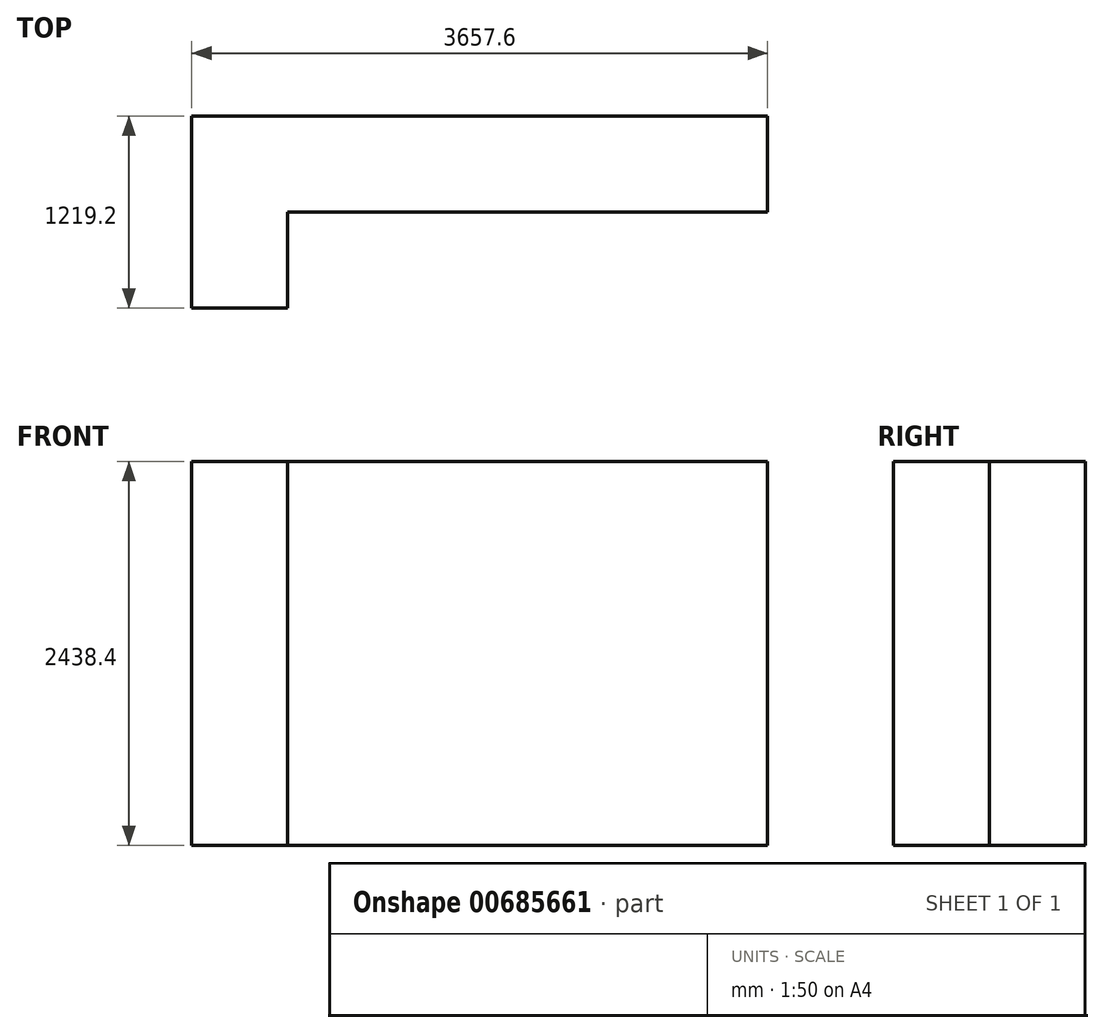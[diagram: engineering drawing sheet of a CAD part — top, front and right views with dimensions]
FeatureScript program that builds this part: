
annotation { "Feature Type Name" : "Feature", "Feature Type Description" : "" }
export const myFeature = defineFeature(function(context is Context, id is Id, definition is map)
    precondition{}
    {
        {
            var Q0;
            Q0=qCreatedBy(makeId("Top.planeOp"),FACE);
            var sketch = newSketch(context, id + "F0", { "sketchPlane" : qUnion([Q0])});
            skLineSegment(sketch, "E0", {"start": v(0, 0) * mm, "end": v(0, 609.6) * mm});
            skLineSegment(sketch, "E1", {"start": v(0, 609.6) * mm, "end": v(3048, 609.6) * mm});
            skLineSegment(sketch, "E2", {"start": v(3048, 609.6) * mm, "end": v(3048, 1219.2) * mm});
            skLineSegment(sketch, "E3", {"start": v(3048, 1219.2) * mm, "end": v(-609.6, 1219.2) * mm});
            skLineSegment(sketch, "E4", {"start": v(-609.6, 1219.2) * mm, "end": v(-609.6, 0) * mm});
            skLineSegment(sketch, "E5", {"start": v(-609.6, 0) * mm, "end": v(0, 0) * mm});
            skSolve(sketch);
        }
        {
            var Q0;
            Q0 = qSketchRegion(id + "F0", true);
            extrude(context, id + "F1", {"entities" : qUnion([Q0]), "depth" : 2438.4 * mm, "offsetDistance" : 30.48 * mm});
        }
    });
